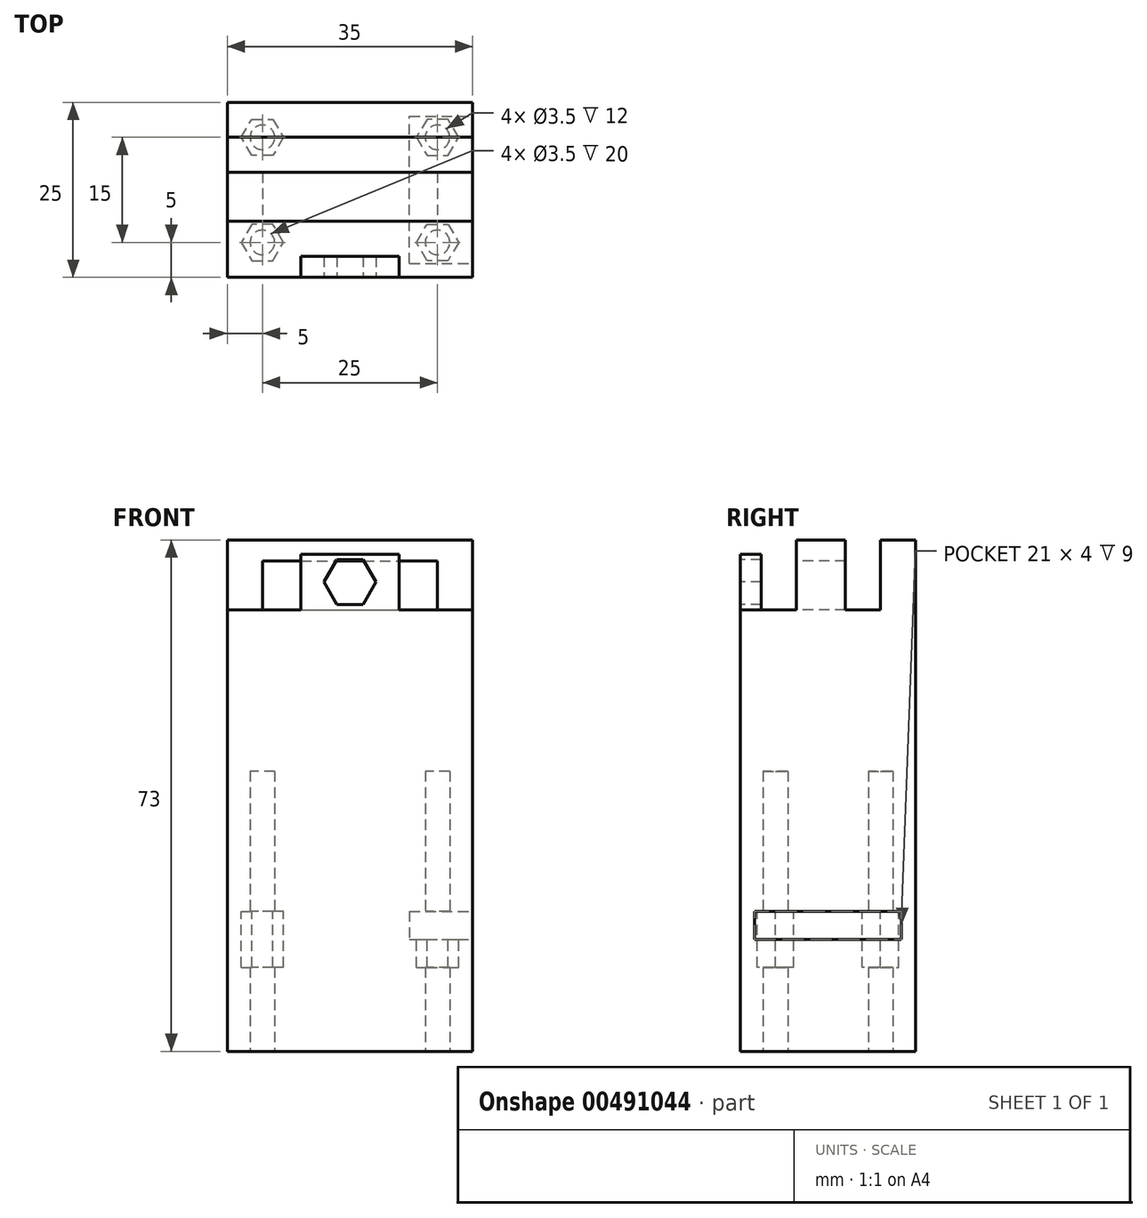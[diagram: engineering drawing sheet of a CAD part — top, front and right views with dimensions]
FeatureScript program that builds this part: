
annotation { "Feature Type Name" : "Feature", "Feature Type Description" : "" }
export const myFeature = defineFeature(function(context is Context, id is Id, definition is map)
    precondition{}
    {
        {
            var Q0;
            Q0=qCreatedBy(makeId("Top.planeOp"),FACE);
            var sketch = newSketch(context, id + "F0", { "sketchPlane" : qUnion([Q0])});
            skLineSegment(sketch, "E0.bottom", {"start": v(-17.5, 12.5) * mm, "end": v(17.5, 12.5) * mm});
            skLineSegment(sketch, "E0.top", {"start": v(-17.5, -12.5) * mm, "end": v(17.5, -12.5) * mm});
            skLineSegment(sketch, "E0.left", {"start": v(-17.5, 12.5) * mm, "end": v(-17.5, -12.5) * mm});
            skLineSegment(sketch, "E0.right", {"start": v(17.5, 12.5) * mm, "end": v(17.5, -12.5) * mm});
            skCircle(sketch, "E1", {"center": v(-12.5, -7.5) * mm, "radius": 1.75 * mm});
            skCircle(sketch, "E2.MirrorC", {"center": v(-12.5, 7.5) * mm, "radius": 1.75 * mm});
            skCircle(sketch, "E3.MirrorC", {"center": v(12.5, -7.5) * mm, "radius": 1.75 * mm});
            skCircle(sketch, "E4.MirrorC", {"center": v(12.5, 7.5) * mm, "radius": 1.75 * mm});
            skSolve(sketch);
        }
        {
            var Q0;
            Q0=qSketchRegion(id+"F0",true);
            extrude(context, id + "F1", {"entities" : qUnion([Q0]), "depth" : 40 * mm});
        }
        {
            var Q0;
            Q0=makeQuery(id+"F1.opExtrude","CAP_FACE",FACE,{"disambiguationData":[OSD([sQuery(id+"F0.wireOp",EDGE,"E0.bottom"),sQuery(id+"F0.wireOp",EDGE,"E0.top"),sQuery(id+"F0.wireOp",EDGE,"E0.left"),sQuery(id+"F0.wireOp",EDGE,"E0.right"),sQuery(id+"F0.wireOp",EDGE,"e4B4wCAe-Tom1-jjty-YN3q-WBH4D0XrJQ7k")])],"isStart":false});
            var sketch = newSketch(context, id + "F2", { "sketchPlane" : qUnion([Q0])});
            skLineSegment(sketch, "E5.bottom", {"start": v(-17.5, 12.5) * mm, "end": v(17.5, 12.5) * mm});
            skLineSegment(sketch, "E5.top", {"start": v(-17.5, -12.5) * mm, "end": v(17.5, -12.5) * mm});
            skLineSegment(sketch, "E5.left", {"start": v(-17.5, 12.5) * mm, "end": v(-17.5, -12.5) * mm});
            skLineSegment(sketch, "E5.right", {"start": v(17.5, 12.5) * mm, "end": v(17.5, -12.5) * mm});
            skSolve(sketch);
        }
        {
            var Q0;
            Q0=qSketchRegion(id+"F2",true);
            extrude(context, id + "F3", {"entities" : qUnion([Q0]), "operationType" : NewBodyOperationType.ADD, "depth" : 23 * mm});
        }
        {
            var Q0;
            Q0=makeQuery(id+"F3.opExtrude","CAP_FACE",FACE,{"disambiguationData":[OSD([sQuery(id+"F2.wireOp",EDGE,"E5.bottom"),sQuery(id+"F2.wireOp",EDGE,"E5.top"),sQuery(id+"F2.wireOp",EDGE,"E5.left"),sQuery(id+"F2.wireOp",EDGE,"E5.right")])],"isStart":false});
            var sketch = newSketch(context, id + "F4", { "sketchPlane" : qUnion([Q0])});
            skLineSegment(sketch, "E6.bottom", {"start": v(-17.5, 12.5) * mm, "end": v(17.5, 12.5) * mm});
            skLineSegment(sketch, "E6.top", {"start": v(-17.5, 7.5) * mm, "end": v(17.5, 7.5) * mm});
            skLineSegment(sketch, "E6.left", {"start": v(-17.5, 12.5) * mm, "end": v(-17.5, 7.5) * mm});
            skLineSegment(sketch, "E6.right", {"start": v(17.5, 12.5) * mm, "end": v(17.5, 7.5) * mm});
            skSolve(sketch);
        }
        {
            var Q0;
            Q0=qSketchRegion(id+"F4",true);
            extrude(context, id + "F5", {"entities" : qUnion([Q0]), "operationType" : NewBodyOperationType.ADD, "depth" : 10 * mm});
        }
        {
            var Q0;
            Q0=makeQuery(id+"F3.opExtrude","CAP_FACE",FACE,{"disambiguationData":[OSD([sQuery(id+"F2.wireOp",EDGE,"E5.bottom"),sQuery(id+"F2.wireOp",EDGE,"E5.top"),sQuery(id+"F2.wireOp",EDGE,"E5.left"),sQuery(id+"F2.wireOp",EDGE,"E5.right")])],"isStart":false});
            var sketch = newSketch(context, id + "F6", { "sketchPlane" : qUnion([Q0])});
            skLineSegment(sketch, "E7.bottom", {"start": v(-17.5, 2.5) * mm, "end": v(17.5, 2.5) * mm});
            skLineSegment(sketch, "E7.top", {"start": v(-17.5, -4.5) * mm, "end": v(17.5, -4.5) * mm});
            skLineSegment(sketch, "E7.left", {"start": v(-17.5, 2.5) * mm, "end": v(-17.5, -4.5) * mm});
            skLineSegment(sketch, "E7.right", {"start": v(17.5, 2.5) * mm, "end": v(17.5, -4.5) * mm});
            skSolve(sketch);
        }
        {
            var Q0;
            Q0=qSketchRegion(id+"F6",true);
            extrude(context, id + "F7", {"entities" : qUnion([Q0]), "operationType" : NewBodyOperationType.ADD, "depth" : 10 * mm});
        }
        {
            var Q0;
            Q0=makeQuery(id+"F7.opExtrude","SWEPT_FACE",FACE,{"disambiguationData":[OSD([sQuery(id+"F6.wireOp",EDGE,"E7.top")])]});
            var sketch = newSketch(context, id + "F8", { "sketchPlane" : qUnion([Q0])});
            skLineSegment(sketch, "E8.bottom", {"start": v(-12.5, 70) * mm, "end": v(12.5, 70) * mm});
            skLineSegment(sketch, "E8.top", {"start": v(-12.5, 63) * mm, "end": v(12.5, 63) * mm});
            skLineSegment(sketch, "E8.left", {"start": v(-12.5, 70) * mm, "end": v(-12.5, 63) * mm});
            skLineSegment(sketch, "E8.right", {"start": v(12.5, 70) * mm, "end": v(12.5, 63) * mm});
            skSolve(sketch);
        }
        {
            var Q0;
            Q0=qSketchRegion(id+"F8",true);
            extrude(context, id + "F9", {"entities" : qUnion([Q0]), "operationType" : NewBodyOperationType.REMOVE, "oppositeDirection" : true, "depth" : 7 * mm});
        }
        {
            var Q0;
            {var subQ1=sQuery(id+"F2.wireOp",EDGE,"E5.right");var subQ3=sQuery(id+"F2.wireOp",EDGE,"E5.left");var subQ8=sQuery(id+"F2.wireOp",EDGE,"E5.top");var subQ9=makeQuery(id+"F3.opExtrude","CAP_FACE",FACE,{"disambiguationData":[OSD([sQuery(id+"F2.wireOp",EDGE,"E5.bottom"),subQ8,subQ3,subQ1])],"isStart":false});Q0=makeQuery(id+"F9.boolean.opBoolean","MERGE",FACE,{"derivedFrom":[makeQuery(id+"F7.boolean.opBoolean","SPLIT",FACE,{"disambiguationData":[TD([makeQuery(id+"F1.opExtrude","SWEPT_FACE",FACE,{"disambiguationData":[OSD([sQuery(id+"F0.wireOp",EDGE,"E0.top")])]})])],"derivedFrom":subQ9}),makeQuery(id+"F7.boolean.opBoolean","SPLIT",FACE,{"disambiguationData":[TD([makeQuery(id+"F5.opExtrude","SWEPT_FACE",FACE,{"disambiguationData":[OSD([sQuery(id+"F4.wireOp",EDGE,"E6.top")])]})])],"derivedFrom":subQ9}),makeQuery(id+"F9.opExtrude","SWEPT_FACE",FACE,{"disambiguationData":[OSD([sQuery(id+"F8.wireOp",EDGE,"E8.top")])]})]});}
            var sketch = newSketch(context, id + "F10", { "sketchPlane" : qUnion([Q0])});
            skLineSegment(sketch, "E9.bottom", {"start": v(-7, -9.5) * mm, "end": v(7, -9.5) * mm});
            skLineSegment(sketch, "E9.top", {"start": v(-7, -12.5) * mm, "end": v(7, -12.5) * mm});
            skLineSegment(sketch, "E9.left", {"start": v(-7, -9.5) * mm, "end": v(-7, -12.5) * mm});
            skLineSegment(sketch, "E9.right", {"start": v(7, -9.5) * mm, "end": v(7, -12.5) * mm});
            skSolve(sketch);
        }
        {
            var Q0;
            Q0=makeQuery(id+"F10.imprint","IMPRINT",FACE,{"disambiguationData":[TD([[makeQuery(id+"F10.imprint","IMPRINT",EDGE,{"derivedFrom":sQuery(id+"F10.wireOp",EDGE,"E9.bottom")}),-1.0]])]});
            extrude(context, id + "F11", {"entities" : qUnion([Q0]), "operationType" : NewBodyOperationType.ADD, "depth" : 8 * mm});
        }
        {
            var Q0;
            Q0=makeQuery(id+"F11.boolean.opBoolean","MERGE",FACE,{"derivedFrom":[makeQuery(id+"F3.boolean.opBoolean","MERGE",FACE,{"derivedFrom":[makeQuery(id+"F1.opExtrude","SWEPT_FACE",FACE,{"disambiguationData":[OSD([sQuery(id+"F0.wireOp",EDGE,"E0.top")])]}),makeQuery(id+"F3.opExtrude","SWEPT_FACE",FACE,{"disambiguationData":[OSD([sQuery(id+"F2.wireOp",EDGE,"E5.top")])]})]}),makeQuery(id+"F11.opExtrude","SWEPT_FACE",FACE,{"disambiguationData":[OSD([sQuery(id+"F10.wireOp",EDGE,"E9.top")])]})]});
            var sketch = newSketch(context, id + "F12", { "sketchPlane" : qUnion([Q0])});
            skLineSegment(sketch, "E10.bottom", {"start": v(-7, 71) * mm, "end": v(7, 71) * mm});
            skLineSegment(sketch, "E10.top", {"start": v(-7, 63) * mm, "end": v(7, 63) * mm});
            skLineSegment(sketch, "E10.left", {"start": v(-7, 71) * mm, "end": v(-7, 63) * mm});
            skLineSegment(sketch, "E10.right", {"start": v(7, 71) * mm, "end": v(7, 63) * mm});
            skPoint(sketch, "E11.centerSnap0", {"position": v(-7, 67) * mm});
            skCircle(sketch, "E12.cCircle", {"center": v(0, 67) * mm, "radius": 3.22 * mm, "construction": true});
            skLineSegment(sketch, "E12.0", {"start": v(1.86, 70.22) * mm, "end": v(3.72, 67) * mm});
            skLineSegment(sketch, "E12.1", {"start": v(3.72, 67) * mm, "end": v(1.86, 63.78) * mm});
            skLineSegment(sketch, "E12.2", {"start": v(1.86, 63.78) * mm, "end": v(-1.86, 63.78) * mm});
            skLineSegment(sketch, "E12.3", {"start": v(-1.86, 63.78) * mm, "end": v(-3.72, 67) * mm});
            skLineSegment(sketch, "E12.4", {"start": v(-3.72, 67) * mm, "end": v(-1.86, 70.22) * mm});
            skLineSegment(sketch, "E12.5", {"start": v(-1.86, 70.22) * mm, "end": v(1.86, 70.22) * mm});
            skPoint(sketch, "E12.0.midPoint", {"position": v(2.79, 68.6) * mm});
            skSolve(sketch);
        }
        {
            var Q0;
            Q0=qCreatedBy(makeId("Top.planeOp"),FACE);
            cPlane(context, id + "F13", {"entities" : qUnion([Q0]), "cplaneType" : CPlaneType.OFFSET, "offset" : 20 * mm, "width" : 150 * mm, "height" : 150 * mm});
        }
        {
            var Q0;
            Q0=qCreatedBy(id+"F13.planeOp",FACE);
            var sketch = newSketch(context, id + "F14", { "sketchPlane" : qUnion([Q0])});
            skCircle(sketch, "E13.cCircle", {"center": v(12.5, -7.5) * mm, "radius": 2.6 * mm, "construction": true});
            skLineSegment(sketch, "E13.0", {"start": v(15.5, -7.5) * mm, "end": v(14, -10.1) * mm});
            skLineSegment(sketch, "E13.1", {"start": v(14, -10.1) * mm, "end": v(11, -10.1) * mm});
            skLineSegment(sketch, "E13.2", {"start": v(11, -10.1) * mm, "end": v(9.5, -7.5) * mm});
            skLineSegment(sketch, "E13.3", {"start": v(9.5, -7.5) * mm, "end": v(11, -4.9) * mm});
            skLineSegment(sketch, "E13.4", {"start": v(11, -4.9) * mm, "end": v(14, -4.9) * mm});
            skLineSegment(sketch, "E13.5", {"start": v(14, -4.9) * mm, "end": v(15.5, -7.5) * mm});
            skPoint(sketch, "E13.0.midPoint", {"position": v(14.75, -8.8) * mm});
            skPoint(sketch, "E14.MirrorP", {"position": v(12.43, -7.4) * mm});
            skLineSegment(sketch, "E15.MirrorCS", {"start": v(9.5, 7.5) * mm, "end": v(11, 4.9) * mm});
            skLineSegment(sketch, "E16.MirrorCS", {"start": v(14, 4.9) * mm, "end": v(15.5, 7.5) * mm});
            skLineSegment(sketch, "E17.MirrorCS", {"start": v(11, 4.9) * mm, "end": v(14, 4.9) * mm});
            skLineSegment(sketch, "E18.MirrorCS", {"start": v(15.5, 7.5) * mm, "end": v(14, 10.1) * mm});
            skLineSegment(sketch, "E19.MirrorCS", {"start": v(14, 10.1) * mm, "end": v(11, 10.1) * mm});
            skLineSegment(sketch, "E20.MirrorCS", {"start": v(11, 10.1) * mm, "end": v(9.5, 7.5) * mm});
            skCircle(sketch, "E21.MirrorC", {"center": v(12.5, 7.5) * mm, "radius": 2.6 * mm, "construction": true});
            skPoint(sketch, "E22.MirrorP", {"position": v(12.43, 7.4) * mm});
            skPoint(sketch, "E23.MirrorP", {"position": v(14.75, 8.8) * mm});
            skLineSegment(sketch, "E24.MirrorCS", {"start": v(-9.5, 7.5) * mm, "end": v(-11, 4.9) * mm});
            skLineSegment(sketch, "E25.MirrorCS", {"start": v(-15.5, 7.5) * mm, "end": v(-14, 10.1) * mm});
            skLineSegment(sketch, "E26.MirrorCS", {"start": v(-11, 4.9) * mm, "end": v(-14, 4.9) * mm});
            skLineSegment(sketch, "E27.MirrorCS", {"start": v(-11, -10.1) * mm, "end": v(-9.5, -7.5) * mm});
            skLineSegment(sketch, "E28.MirrorCS", {"start": v(-15.5, -7.5) * mm, "end": v(-14, -10.1) * mm});
            skLineSegment(sketch, "E29.MirrorCS", {"start": v(-14, -10.1) * mm, "end": v(-11, -10.1) * mm});
            skLineSegment(sketch, "E30.MirrorCS", {"start": v(-14, 4.9) * mm, "end": v(-15.5, 7.5) * mm});
            skCircle(sketch, "E31.MirrorC", {"center": v(-12.5, 7.5) * mm, "radius": 2.6 * mm, "construction": true});
            skLineSegment(sketch, "E32.MirrorCS", {"start": v(-14, 10.1) * mm, "end": v(-11, 10.1) * mm});
            skLineSegment(sketch, "E33.MirrorCS", {"start": v(-14, -4.9) * mm, "end": v(-15.5, -7.5) * mm});
            skLineSegment(sketch, "E34.MirrorCS", {"start": v(-9.5, -7.5) * mm, "end": v(-11, -4.9) * mm});
            skLineSegment(sketch, "E35.MirrorCS", {"start": v(-11, -4.9) * mm, "end": v(-14, -4.9) * mm});
            skLineSegment(sketch, "E36.MirrorCS", {"start": v(-11, 10.1) * mm, "end": v(-9.5, 7.5) * mm});
            skPoint(sketch, "E37.MirrorP", {"position": v(-12.43, -7.4) * mm});
            skPoint(sketch, "E38.MirrorP", {"position": v(-14.75, -8.8) * mm});
            skPoint(sketch, "E39.MirrorP", {"position": v(-14.75, 8.8) * mm});
            skCircle(sketch, "E40.MirrorC", {"center": v(-12.5, -7.5) * mm, "radius": 2.6 * mm, "construction": true});
            skPoint(sketch, "E41.MirrorP", {"position": v(-12.43, 7.4) * mm});
            skSolve(sketch);
        }
        {
            var Q0;
            Q0 = qSketchRegion(id + "F14", true);
            extrude(context, id + "F15", {"entities" : qUnion([Q0]), "operationType" : NewBodyOperationType.REMOVE, "oppositeDirection" : true, "depth" : 8 * mm});
        }
        {
            var Q0;
            Q0=makeQuery(id+"F7.boolean.opBoolean","MERGE",FACE,{"derivedFrom":[makeQuery(id+"F5.boolean.opBoolean","MERGE",FACE,{"derivedFrom":[makeQuery(id+"F3.boolean.opBoolean","MERGE",FACE,{"derivedFrom":[makeQuery(id+"F1.opExtrude","SWEPT_FACE",FACE,{"disambiguationData":[OSD([sQuery(id+"F0.wireOp",EDGE,"E0.right")])]}),makeQuery(id+"F3.opExtrude","SWEPT_FACE",FACE,{"disambiguationData":[OSD([sQuery(id+"F2.wireOp",EDGE,"E5.right")])]})]}),makeQuery(id+"F5.opExtrude","SWEPT_FACE",FACE,{"disambiguationData":[OSD([sQuery(id+"F4.wireOp",EDGE,"E6.right")])]})]}),makeQuery(id+"F7.opExtrude","SWEPT_FACE",FACE,{"disambiguationData":[OSD([sQuery(id+"F6.wireOp",EDGE,"E7.right")])]})]});
            var sketch = newSketch(context, id + "F16", { "sketchPlane" : qUnion([Q0])});
            skLineSegment(sketch, "E42.bottom", {"start": v(-10.5, 20) * mm, "end": v(10.5, 20) * mm});
            skLineSegment(sketch, "E42.top", {"start": v(-10.5, 16) * mm, "end": v(10.5, 16) * mm});
            skLineSegment(sketch, "E42.left", {"start": v(-10.5, 20) * mm, "end": v(-10.5, 16) * mm});
            skLineSegment(sketch, "E42.right", {"start": v(10.5, 20) * mm, "end": v(10.5, 16) * mm});
            skSolve(sketch);
        }
        {
            var Q0;
            Q0 = qSketchRegion(id + "F16", true);
            extrude(context, id + "F17", {"entities" : qUnion([Q0]), "operationType" : NewBodyOperationType.REMOVE, "oppositeDirection" : true, "depth" : 9 * mm});
        }
        {
            var Q0;
            Q0=makeQuery(id+"F12.imprint","IMPRINT",FACE,{"disambiguationData":[TD([[makeQuery(id+"F12.imprint","IMPRINT",EDGE,{"derivedFrom":sQuery(id+"F12.wireOp",EDGE,"E12.0")}),-1.0]])]});
            extrude(context, id + "F18", {"entities" : qUnion([Q0]), "operationType" : NewBodyOperationType.REMOVE, "oppositeDirection" : true, "depth" : 3 * mm});
        }
    });
